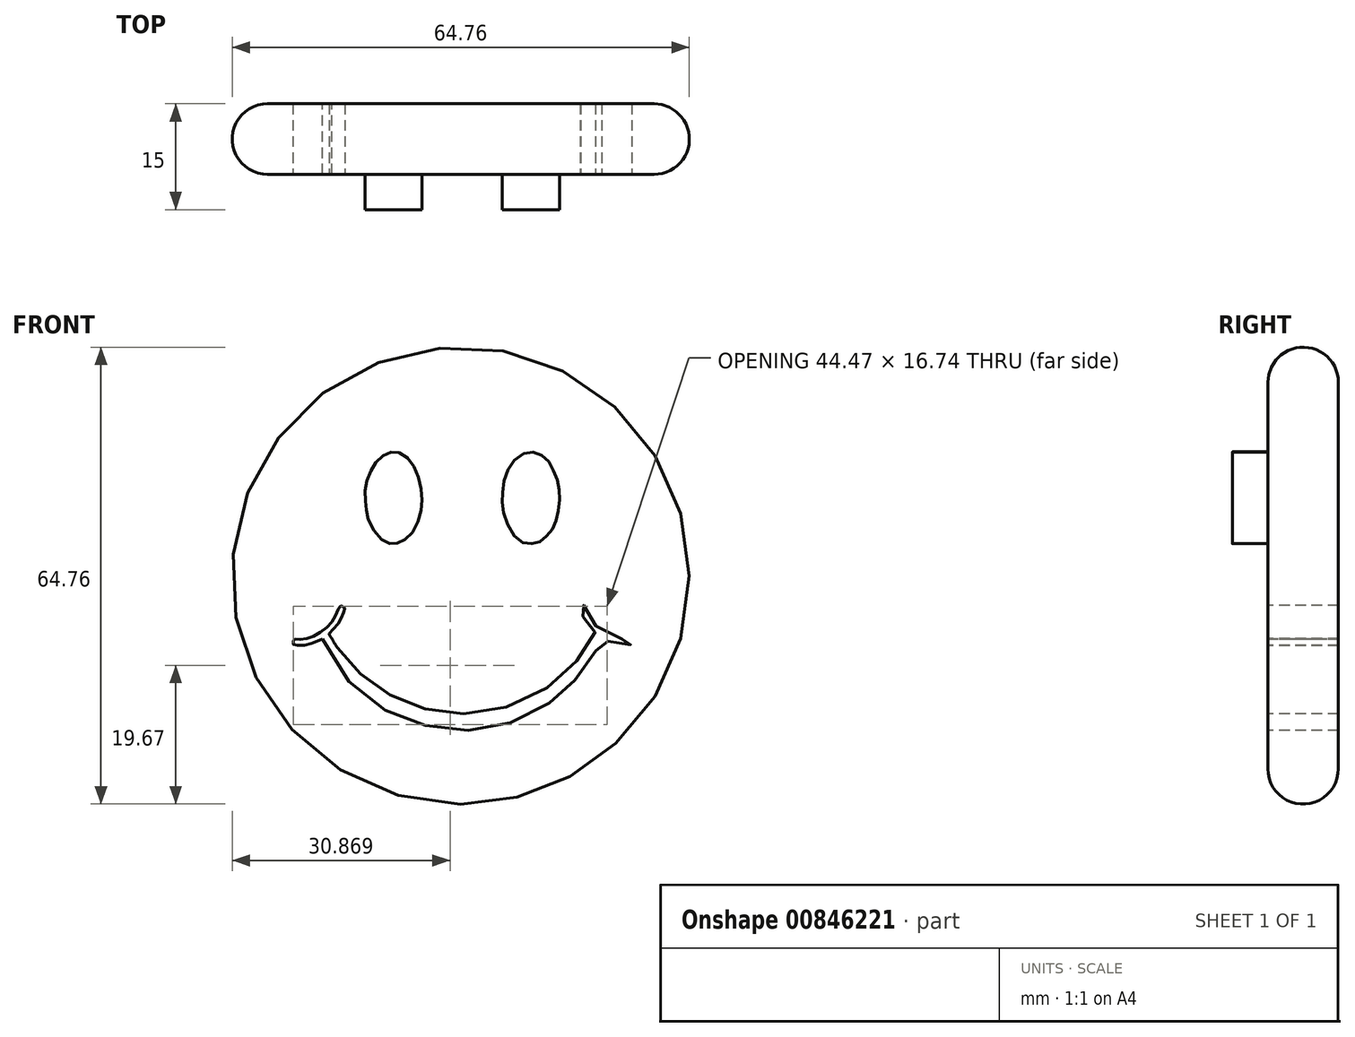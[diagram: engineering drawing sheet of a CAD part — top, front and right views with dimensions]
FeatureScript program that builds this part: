
annotation { "Feature Type Name" : "Feature", "Feature Type Description" : "" }
export const myFeature = defineFeature(function(context is Context, id is Id, definition is map)
    precondition{}
    {
        {
            var Q0;
            Q0=qCreatedBy(makeId("Front.planeOp"),FACE);
            var sketch = newSketch(context, id + "F0", { "sketchPlane" : qUnion([Q0])});
            skCircle(sketch, "E0", {"center": v(0, 0) * mm, "radius": 32.38 * mm});
            skSolve(sketch);
        }
        {
            var Q0;
            Q0=makeQuery(id+"F0.imprint","IMPRINT",FACE,{"disambiguationData":[TD([[makeQuery(id+"F0.imprint","IMPRINT",EDGE,{"derivedFrom":sQuery(id+"F0.wireOp",EDGE,"E0")}),1.0]])]});
            var sketch = newSketch(context, id + "F1", { "sketchPlane" : qUnion([Q0])});
            skFitSpline(sketch, "E1", {"points": [v(-18.61, -8.2) * mm, v(-17.47, -10.21) * mm, v(-15.6, -12.46) * mm, v(-13.55, -14.57) * mm, v(-11.3, -16.21) * mm, v(-7.21, -18.16) * mm, v(-4.9, -18.93) * mm, v(-1.52, -19.5) * mm, v(2.7, -19.4) * mm, v(7.3, -18.36) * mm, v(11.79, -16.18) * mm, v(14.8, -13.77) * mm, v(17.52, -10.65) * mm, v(19.1, -8.14) * mm, v(19.06, -8.07) * mm, v(18.33, -7.5) * mm, v(17.82, -6.76) * mm, v(17.29, -5.76) * mm, v(16.95, -4.82) * mm, v(16.98, -4.58) * mm, v(16.95, -4.32) * mm, v(17.29, -4.22) * mm, v(17.49, -4.25) * mm, v(17.86, -5.22) * mm, v(18.9, -6.8) * mm, v(20.24, -8.1) * mm, v(22.28, -8.94) * mm, v(23.89, -9.04) * mm, v(24.09, -9.2) * mm, v(24.22, -9.38) * mm, v(24.22, -9.54) * mm, v(24.09, -9.75) * mm, v(23.86, -9.88) * mm, v(22.58, -9.85) * mm, v(20.9, -9.34) * mm, v(19.97, -8.94) * mm, v(19.97, -9.08) * mm, v(19.87, -9.3) * mm, v(18.66, -11.59) * mm, v(16.95, -13.94) * mm, v(14.57, -16.48) * mm, v(12.73, -17.96) * mm, v(8.5, -20.3) * mm, v(4.88, -21.4) * mm, v(0, -21.95) * mm, v(-4.27, -21.38) * mm, v(-8.42, -20.27) * mm, v(-12.51, -17.86) * mm, v(-16.73, -13.87) * mm, v(-19.58, -8.97) * mm, v(-19.68, -9) * mm, v(-19.75, -9) * mm], "startDerivative": vector(45.89, -90.94) * mm, "endDerivative": vector(-17.8, 3.96) * mm});
            skFitSpline(sketch, "E2", {"points": [v(-19.58, -8.97) * mm, v(-20.62, -9.41) * mm, v(-21.93, -9.81) * mm, v(-23.4, -9.85) * mm, v(-23.74, -9.68) * mm, v(-23.74, -9.34) * mm, v(-23.6, -9) * mm, v(-23.3, -9) * mm, v(-22.1, -9) * mm, v(-20.65, -8.47) * mm, v(-18.88, -7.3) * mm, v(-17.87, -6) * mm, v(-17.34, -4.68) * mm, v(-17.2, -4.48) * mm, v(-16.97, -4.25) * mm, v(-16.83, -4.28) * mm, v(-16.46, -4.55) * mm, v(-16.57, -5.12) * mm, v(-16.97, -6.06) * mm, v(-17.7, -7.23) * mm, v(-18.61, -8.2) * mm, v(-18.27, -8.87) * mm, v(-17.47, -10.21) * mm], "startDerivative": vector(-19.63, -8.38) * mm, "endDerivative": vector(12.89, -23.79) * mm});
            skSolve(sketch);
        }
        {
            var Q0;
            Q0=makeQuery(id+"F0.imprint","IMPRINT",FACE,{"disambiguationData":[TD([[makeQuery(id+"F0.imprint","IMPRINT",EDGE,{"derivedFrom":sQuery(id+"F0.wireOp",EDGE,"E0")}),1.0]])]});
            var sketch = newSketch(context, id + "F2", { "sketchPlane" : qUnion([Q0])});
            skFitSpline(sketch, "E3", {"points": [v(-13.08, 7.98) * mm, v(-13.43, 9.82) * mm, v(-13.55, 11.98) * mm, v(-13.04, 14.14) * mm, v(-11.98, 16.06) * mm, v(-10.45, 17.32) * mm, v(-9.08, 17.51) * mm, v(-7.31, 16.41) * mm, v(-6.02, 14.1) * mm, v(-5.5, 11.2) * mm, v(-5.7, 8.68) * mm, v(-7, 5.94) * mm, v(-8.57, 4.76) * mm, v(-9.86, 4.53) * mm, v(-11.31, 5.23) * mm, v(-13.08, 7.98) * mm]});
            skFitSpline(sketch, "E4", {"points": [v(6.61, 7.27) * mm, v(5.9, 9.78) * mm, v(5.9, 11.59) * mm, v(6.34, 14.14) * mm, v(7.56, 16.33) * mm, v(9.48, 17.47) * mm, v(11, 17.32) * mm, v(12.38, 16.3) * mm, v(13.24, 14.65) * mm, v(13.87, 12.76) * mm, v(13.99, 10.96) * mm, v(13.75, 8.68) * mm, v(13.2, 7) * mm, v(12.34, 5.78) * mm, v(11.24, 4.84) * mm, v(9.9, 4.53) * mm, v(8.38, 4.88) * mm, v(6.61, 7.27) * mm]});
            skSolve(sketch);
        }
        {
            var Q0;
            Q0 = qSketchRegion(id + "F0", true);
            extrude(context, id + "F3", {"entities" : qUnion([Q0]), "depth" : 10 * mm, "offsetDistance" : 25 * mm});
        }
        {
            var Q0;
            Q0=makeQuery(id+"F2.imprint","IMPRINT",FACE,{"disambiguationData":[TD([[makeQuery(id+"F2.imprint","IMPRINT",EDGE,{"derivedFrom":sQuery(id+"F2.wireOp",EDGE,"E4")}),-1.0]])]});
            var Q1;
            Q1=makeQuery(id+"F2.imprint","IMPRINT",FACE,{"disambiguationData":[TD([[makeQuery(id+"F2.imprint","IMPRINT",EDGE,{"derivedFrom":sQuery(id+"F2.wireOp",EDGE,"E3")}),-1.0]])]});
            extrude(context, id + "F4", {"entities" : qUnion([Q0, Q1]), "operationType" : NewBodyOperationType.ADD, "depth" : 15 * mm, "offsetDistance" : 25 * mm});
        }
        {
            var Q0;
            {var subQ0=sQuery(id+"F1.wireOp",EDGE,"E2");var subQ1=sQuery(id+"F1.wireOp",EDGE,"E1");var subQ2=makeQuery(id+"F1.imprint","INTERSECT",VERTEX,{"disambiguationData":[OD(2.0)],"derivedFrom":[subQ1,subQ0]});Q0=makeQuery(id+"F1.imprint","IMPRINT",FACE,{"disambiguationData":[TD([[makeQuery(id+"F1.imprint","IMPRINT",EDGE,{"disambiguationData":[TD([[subQ2,1.0]])],"derivedFrom":subQ1}),-1.0]])]});}
            extrude(context, id + "F5", {"entities" : qUnion([Q0]), "operationType" : NewBodyOperationType.REMOVE, "depth" : 25 * mm, "offsetDistance" : 25 * mm});
        }
        {
            var Q0;
            Q0=makeQuery(id+"F3.opExtrude","SWEPT_FACE",FACE,{"disambiguationData":[OSD([sQuery(id+"F0.wireOp",EDGE,"E0")])]});
            fillet(context, id + "F6", {"entities" : qUnion([Q0]), "radius" : 5 * mm, "tangentPropagation" : true, "allowEdgeOverflow" : false});
        }
    });
